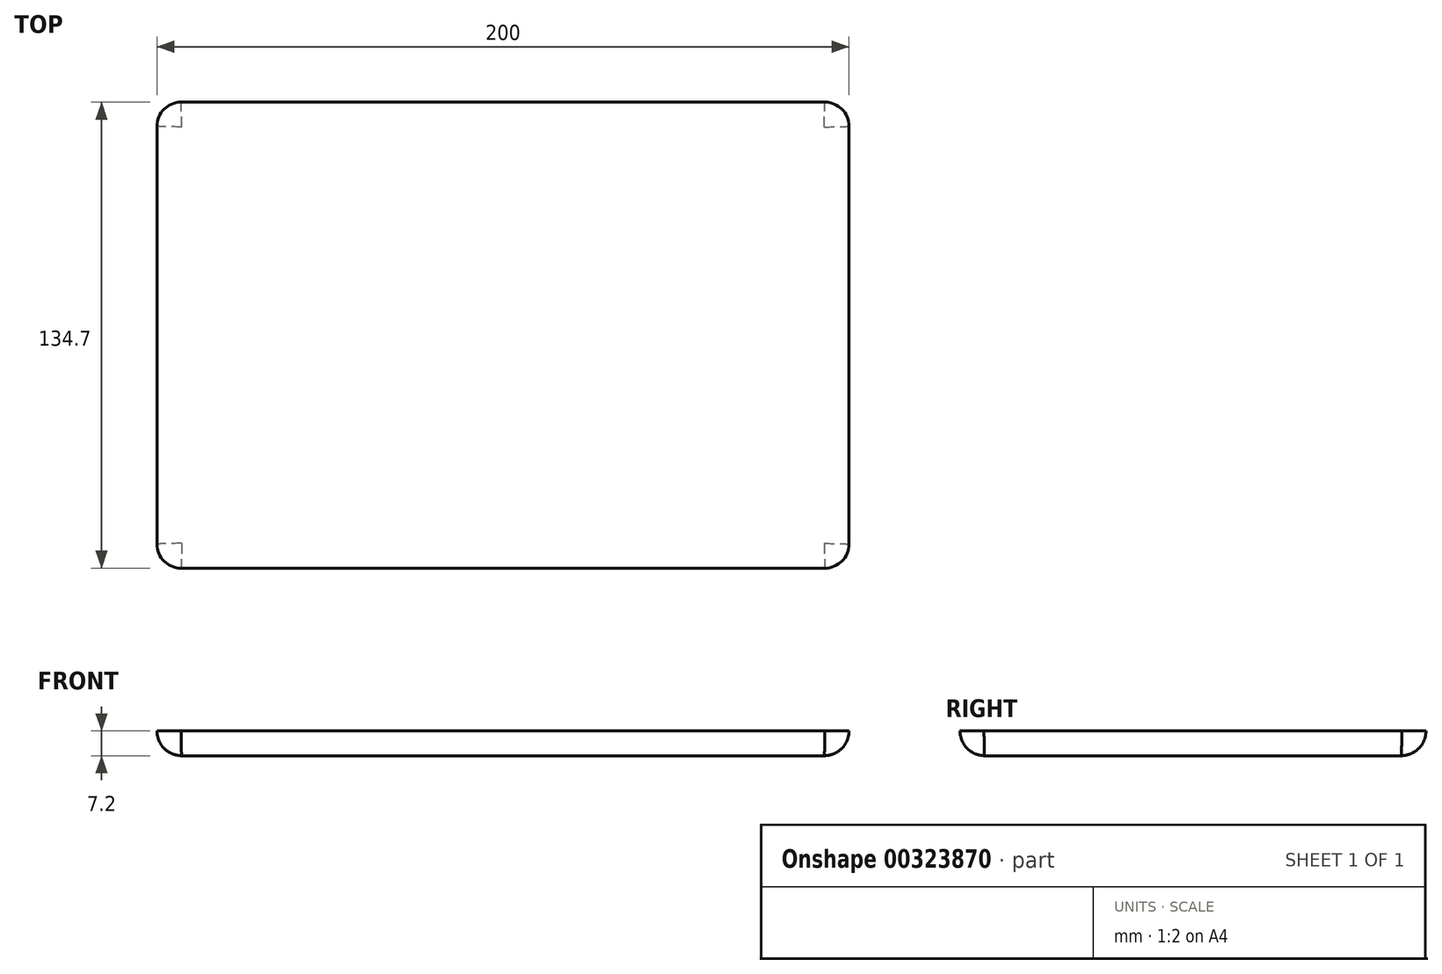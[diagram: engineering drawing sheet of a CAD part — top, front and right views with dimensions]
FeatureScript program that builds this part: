
annotation { "Feature Type Name" : "Feature", "Feature Type Description" : "" }
export const myFeature = defineFeature(function(context is Context, id is Id, definition is map)
    precondition{}
    {
        {
            var Q0;
            Q0=qCreatedBy(makeId("Top.planeOp"),FACE);
            var sketch = newSketch(context, id + "F0", { "sketchPlane" : qUnion([Q0])});
            skLineSegment(sketch, "E0.bottom", {"start": v(100, 67.35) * mm, "end": v(-100, 67.35) * mm});
            skLineSegment(sketch, "E0.top", {"start": v(100, -67.35) * mm, "end": v(-100, -67.35) * mm});
            skLineSegment(sketch, "E0.left", {"start": v(100, 67.35) * mm, "end": v(100, -67.35) * mm});
            skLineSegment(sketch, "E0.right", {"start": v(-100, 67.35) * mm, "end": v(-100, -67.35) * mm});
            skPoint(sketch, "E0.middle", {"position": v(0, 0) * mm});
            skSolve(sketch);
        }
        {
            var Q0;
            Q0=makeQuery(id+"F0.imprint","IMPRINT",FACE,{"disambiguationData":[TD([[makeQuery(id+"F0.imprint","IMPRINT",EDGE,{"derivedFrom":sQuery(id+"F0.wireOp",EDGE,"E0.bottom")}),1.0]])]});
            extrude(context, id + "F1", {"entities" : qUnion([Q0]), "depth" : 7.2 * mm});
        }
        {
            var Q0;
            Q0=makeQuery(id+"F1.opExtrude","SWEPT_EDGE",EDGE,{"disambiguationData":[OSD([sQuery(id+"F0.wireOp",EDGE,"E0.top"),sQuery(id+"F0.wireOp",EDGE,"E0.right")])]});
            var Q1;
            Q1=makeQuery(id+"F1.opExtrude","SWEPT_EDGE",EDGE,{"disambiguationData":[OSD([sQuery(id+"F0.wireOp",EDGE,"E0.top"),sQuery(id+"F0.wireOp",EDGE,"E0.left")])]});
            var Q2;
            Q2=makeQuery(id+"F1.opExtrude","SWEPT_EDGE",EDGE,{"disambiguationData":[OSD([sQuery(id+"F0.wireOp",EDGE,"E0.bottom"),sQuery(id+"F0.wireOp",EDGE,"E0.left")])]});
            var Q3;
            Q3=makeQuery(id+"F1.opExtrude","SWEPT_EDGE",EDGE,{"disambiguationData":[OSD([sQuery(id+"F0.wireOp",EDGE,"E0.bottom"),sQuery(id+"F0.wireOp",EDGE,"E0.right")])]});
            fillet(context, id + "F2", {"entities" : qUnion([Q0, Q1, Q2, Q3]), "radius" : 7 * mm, "tangentPropagation" : true, "allowEdgeOverflow" : false});
        }
        {
            var Q0;
            Q0=makeQuery(id+"F1.opExtrude","CAP_EDGE",EDGE,{"disambiguationData":[OSD([sQuery(id+"F0.wireOp",EDGE,"E0.top")])],"isStart":true});
            fillet(context, id + "F3", {"entities" : qUnion([Q0]), "radius" : 7.2 * mm, "tangentPropagation" : true, "allowEdgeOverflow" : false});
        }
    });
